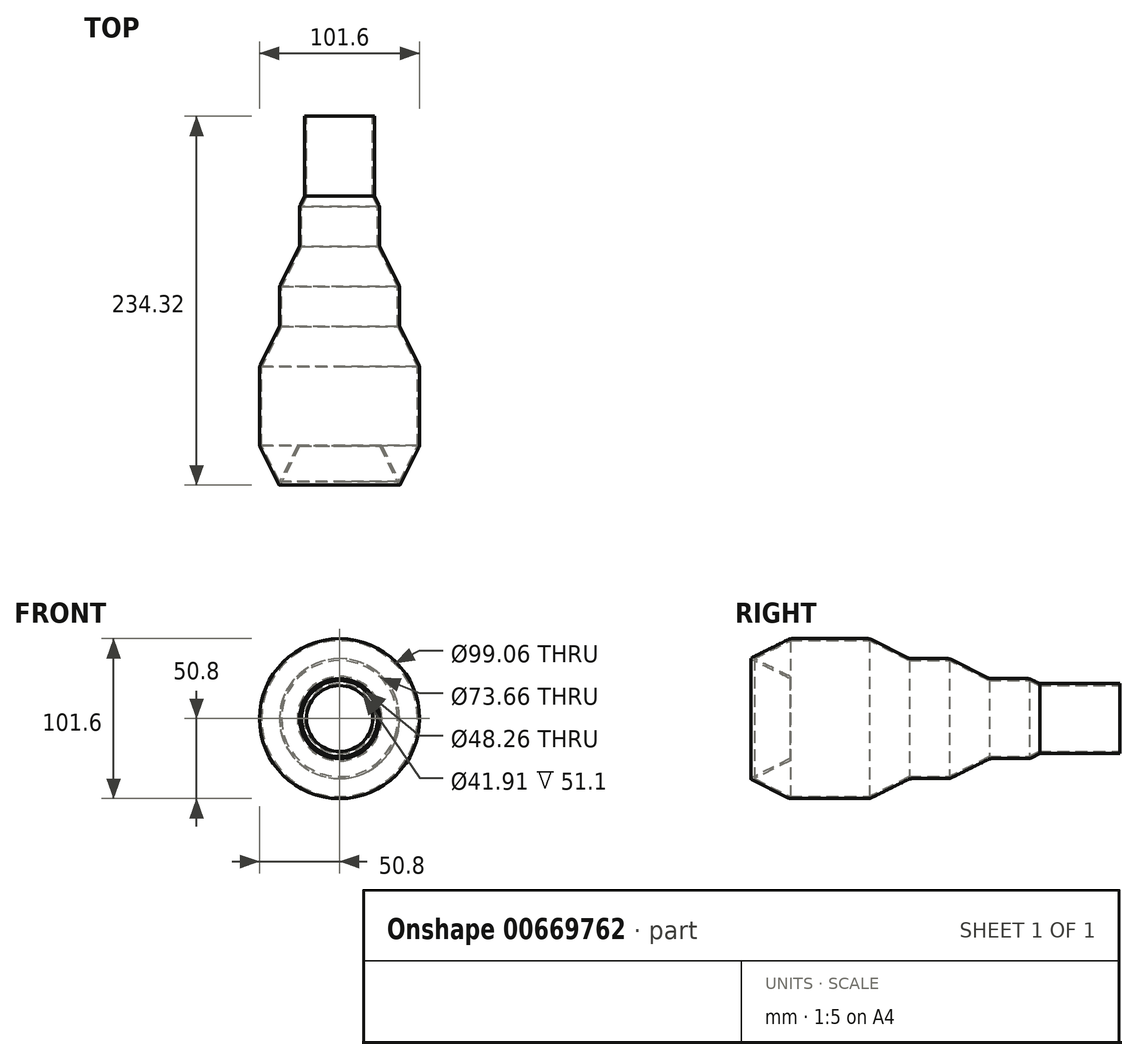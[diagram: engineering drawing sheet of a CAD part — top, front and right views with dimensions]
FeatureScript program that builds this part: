
annotation { "Feature Type Name" : "Feature", "Feature Type Description" : "" }
export const myFeature = defineFeature(function(context is Context, id is Id, definition is map)
    precondition{}
    {
        {
            var Q0;
            Q0=qCreatedBy(makeId("Right.planeOp"),FACE);
            var sketch = newSketch(context, id + "F0", { "sketchPlane" : qUnion([Q0])});
            skLineSegment(sketch, "E0", {"start": v(-199.49, 0) * mm, "end": v(219.8, 0) * mm, "construction": true});
            skLineSegment(sketch, "E1", {"start": v(-135.4, 50.8) * mm, "end": v(-84.6, 50.8) * mm});
            skLineSegment(sketch, "E2", {"start": v(-84.6, 50.8) * mm, "end": v(-59.2, 38.1) * mm});
            skLineSegment(sketch, "E3", {"start": v(-59.2, 38.1) * mm, "end": v(-33.8, 38.1) * mm});
            skLineSegment(sketch, "E4", {"start": v(-33.8, 38.1) * mm, "end": v(-8.4, 25.4) * mm});
            skLineSegment(sketch, "E5", {"start": v(-8.4, 25.4) * mm, "end": v(17, 25.4) * mm});
            skLineSegment(sketch, "E6", {"start": v(17, 25.4) * mm, "end": v(23.35, 22.23) * mm});
            skLineSegment(sketch, "E7", {"start": v(23.35, 22.23) * mm, "end": v(74.15, 22.23) * mm});
            skLineSegment(sketch, "E8", {"start": v(-135.4, 50.8) * mm, "end": v(-160.8, 38.1) * mm});
            skLineSegment(sketch, "E9", {"start": v(-160.8, 38.1) * mm, "end": v(-135.4, 25.4) * mm});
            skLineSegment(sketch, "E10", {"start": v(-84.6, 50.8) * mm, "end": v(-84.6, 0) * mm, "construction": true});
            skLineSegment(sketch, "E11", {"start": v(-59.2, 38.1) * mm, "end": v(-59.2, 0) * mm, "construction": true});
            skLineSegment(sketch, "E12", {"start": v(-33.8, 38.1) * mm, "end": v(-33.8, 0) * mm, "construction": true});
            skLineSegment(sketch, "E13", {"start": v(-8.4, 25.4) * mm, "end": v(-8.4, 0) * mm, "construction": true});
            skLineSegment(sketch, "E14", {"start": v(17, 25.4) * mm, "end": v(17, 0) * mm, "construction": true});
            skLineSegment(sketch, "E15", {"start": v(23.35, 22.23) * mm, "end": v(23.35, 0) * mm, "construction": true});
            skLineSegment(sketch, "E16", {"start": v(-135.4, 50.8) * mm, "end": v(-135.4, 0) * mm, "construction": true});
            skLineSegment(sketch, "E17", {"start": v(-160.8, 38.1) * mm, "end": v(-160.8, 0) * mm, "construction": true});
            skLineSegment(sketch, "E18", {"start": v(74.15, 22.23) * mm, "end": v(74.15, 0) * mm});
            skLineSegment(sketch, "E19.0", {"start": v(-157.96, 38.1) * mm, "end": v(-135.4, 26.82) * mm});
            skLineSegment(sketch, "E19.1", {"start": v(-135.1, 49.53) * mm, "end": v(-157.96, 38.1) * mm});
            skLineSegment(sketch, "E19.2", {"start": v(-135.1, 49.53) * mm, "end": v(-84.9, 49.53) * mm});
            skLineSegment(sketch, "E19.3", {"start": v(-84.9, 49.53) * mm, "end": v(-59.5, 36.83) * mm});
            skLineSegment(sketch, "E19.4", {"start": v(-59.5, 36.83) * mm, "end": v(-34.1, 36.83) * mm});
            skLineSegment(sketch, "E19.5", {"start": v(23.05, 20.95) * mm, "end": v(74.15, 20.95) * mm});
            skLineSegment(sketch, "E19.6", {"start": v(16.7, 24.13) * mm, "end": v(23.05, 20.95) * mm});
            skLineSegment(sketch, "E19.7", {"start": v(-8.7, 24.13) * mm, "end": v(16.7, 24.13) * mm});
            skLineSegment(sketch, "E19.8", {"start": v(-34.1, 36.83) * mm, "end": v(-8.7, 24.13) * mm});
            skLineSegment(sketch, "E20", {"start": v(-135.4, 26.82) * mm, "end": v(-135.4, 25.4) * mm});
            skLineSegment(sketch, "E21.MirrorCS", {"start": v(16.7, -24.13) * mm, "end": v(23.05, -20.95) * mm});
            skLineSegment(sketch, "E22.MirrorCS", {"start": v(17, -25.4) * mm, "end": v(23.35, -22.22) * mm});
            skLineSegment(sketch, "E23.MirrorCS", {"start": v(-135.4, -26.82) * mm, "end": v(-135.4, -25.4) * mm});
            skLineSegment(sketch, "E24.MirrorCS", {"start": v(-135.1, -49.53) * mm, "end": v(-157.96, -38.1) * mm});
            skLineSegment(sketch, "E25.MirrorCS", {"start": v(-84.9, -49.53) * mm, "end": v(-59.5, -36.83) * mm});
            skLineSegment(sketch, "E26.MirrorCS", {"start": v(-59.5, -36.83) * mm, "end": v(-34.1, -36.83) * mm});
            skLineSegment(sketch, "E27.MirrorCS", {"start": v(-34.1, -36.83) * mm, "end": v(-8.7, -24.13) * mm});
            skLineSegment(sketch, "E28.MirrorCS", {"start": v(-135.4, -50.8) * mm, "end": v(-160.8, -38.1) * mm});
            skLineSegment(sketch, "E29.MirrorCS", {"start": v(-160.8, -38.1) * mm, "end": v(-135.4, -25.4) * mm});
            skLineSegment(sketch, "E30.MirrorCS", {"start": v(23.35, -22.23) * mm, "end": v(74.15, -22.23) * mm});
            skLineSegment(sketch, "E31.MirrorCS", {"start": v(-59.2, -38.1) * mm, "end": v(-33.8, -38.1) * mm});
            skLineSegment(sketch, "E32.MirrorCS", {"start": v(-33.8, -38.1) * mm, "end": v(-8.4, -25.4) * mm});
            skLineSegment(sketch, "E33.MirrorCS", {"start": v(-8.4, -25.4) * mm, "end": v(17, -25.4) * mm});
            skLineSegment(sketch, "E34.MirrorCS", {"start": v(-135.4, -50.8) * mm, "end": v(-84.6, -50.8) * mm});
            skLineSegment(sketch, "E35.MirrorCS", {"start": v(-84.6, -50.8) * mm, "end": v(-59.2, -38.1) * mm});
            skLineSegment(sketch, "E36.MirrorCS", {"start": v(-8.7, -24.13) * mm, "end": v(16.7, -24.13) * mm});
            skLineSegment(sketch, "E37.MirrorCS", {"start": v(-157.96, -38.1) * mm, "end": v(-135.4, -26.82) * mm});
            skLineSegment(sketch, "E38.MirrorCS", {"start": v(23.05, -20.95) * mm, "end": v(74.15, -20.95) * mm});
            skLineSegment(sketch, "E39.MirrorCS", {"start": v(-135.1, -49.53) * mm, "end": v(-84.9, -49.53) * mm});
            skLineSegment(sketch, "E40.MirrorCS", {"start": v(74.15, -22.23) * mm, "end": v(74.15, 0) * mm});
            skLineSegment(sketch, "E41", {"start": v(74.15, 20.95) * mm, "end": v(74.15, 20.95) * mm});
            skSolve(sketch);
        }
        {
            var Q0;
            Q0=qCreatedBy(makeId("Front.planeOp"),FACE);
            var sketch = newSketch(context, id + "F1", { "sketchPlane" : qUnion([Q0])});
            skCircle(sketch, "E42", {"center": v(0, 0) * mm, "radius": 50.8 * mm});
            skCircle(sketch, "E43.0", {"center": v(0, 0) * mm, "radius": 50.04 * mm});
            skSolve(sketch);
        }
        {
            var Q0;
            Q0 = qSketchRegion(id + "F0", true);
            var Q1;
            Q1=sQuery(id+"F1.wireOp",EDGE,"E43.0");
            revolve(context, id + "F2", {"entities" : qUnion([Q0]), "axis" : qUnion([Q1]), "revolveType" : RevolveType.FULL});
        }
        {
            var Q0;
            Q0=makeQuery(id+"F2.opRevolve","SWEPT_BODY",BODY,{"disambiguationData":[OSD([sQuery(id+"F0.wireOp",EDGE,"E21.MirrorCS"),sQuery(id+"F0.wireOp",EDGE,"E22.MirrorCS"),sQuery(id+"F0.wireOp",EDGE,"E23.MirrorCS"),sQuery(id+"F0.wireOp",EDGE,"E24.MirrorCS"),sQuery(id+"F0.wireOp",EDGE,"E25.MirrorCS"),sQuery(id+"F0.wireOp",EDGE,"E26.MirrorCS"),sQuery(id+"F0.wireOp",EDGE,"E27.MirrorCS"),sQuery(id+"F0.wireOp",EDGE,"E28.MirrorCS"),sQuery(id+"F0.wireOp",EDGE,"E29.MirrorCS"),sQuery(id+"F0.wireOp",EDGE,"E30.MirrorCS"),sQuery(id+"F0.wireOp",EDGE,"E31.MirrorCS"),sQuery(id+"F0.wireOp",EDGE,"E32.MirrorCS"),sQuery(id+"F0.wireOp",EDGE,"E33.MirrorCS"),sQuery(id+"F0.wireOp",EDGE,"E34.MirrorCS"),sQuery(id+"F0.wireOp",EDGE,"E35.MirrorCS"),sQuery(id+"F0.wireOp",EDGE,"E36.MirrorCS"),sQuery(id+"F0.wireOp",EDGE,"E37.MirrorCS"),sQuery(id+"F0.wireOp",EDGE,"E38.MirrorCS"),sQuery(id+"F0.wireOp",EDGE,"E39.MirrorCS"),sQuery(id+"F0.wireOp",EDGE,"E40.MirrorCS")])]});
            deleteBodies(context, id + "F3", {"entities" : qUnion([Q0])});
        }
        {
            var Q0;
            Q0=makeQuery(id+"F2.opRevolve","SWEPT_EDGE",EDGE,{"disambiguationData":[OSD([sQuery(id+"F0.wireOp",EDGE,"E1"),sQuery(id+"F0.wireOp",EDGE,"E8")])]});
            var Q1;
            Q1=makeQuery(id+"F2.opRevolve","SWEPT_EDGE",EDGE,{"disambiguationData":[OSD([sQuery(id+"F0.wireOp",EDGE,"E1"),sQuery(id+"F0.wireOp",EDGE,"E2")])]});
            var Q2;
            Q2=makeQuery(id+"F2.opRevolve","SWEPT_EDGE",EDGE,{"disambiguationData":[OSD([sQuery(id+"F0.wireOp",EDGE,"E3"),sQuery(id+"F0.wireOp",EDGE,"E4")])]});
            var Q3;
            Q3=makeQuery(id+"F2.opRevolve","SWEPT_EDGE",EDGE,{"disambiguationData":[OSD([sQuery(id+"F0.wireOp",EDGE,"E5"),sQuery(id+"F0.wireOp",EDGE,"E6")])]});
            fillet(context, id + "F4", {"entities" : qUnion([Q0, Q1, Q2, Q3]), "radius" : 5.08 * mm, "tangentPropagation" : true, "allowEdgeOverflow" : false});
        }
        {
            var Q0;
            Q0=makeQuery(id+"F2.opRevolve","SWEPT_EDGE",EDGE,{"disambiguationData":[OSD([sQuery(id+"F0.wireOp",EDGE,"E4"),sQuery(id+"F0.wireOp",EDGE,"E5")])]});
            var Q1;
            Q1=makeQuery(id+"F2.opRevolve","SWEPT_EDGE",EDGE,{"disambiguationData":[OSD([sQuery(id+"F0.wireOp",EDGE,"E2"),sQuery(id+"F0.wireOp",EDGE,"E3")])]});
            fillet(context, id + "F5", {"entities" : qUnion([Q0, Q1]), "radius" : 5.08 * mm, "tangentPropagation" : true, "allowEdgeOverflow" : false});
        }
        {
            var Q0;
            Q0=makeQuery(id+"F2.opRevolve","SWEPT_EDGE",EDGE,{"disambiguationData":[OSD([sQuery(id+"F0.wireOp",EDGE,"E8"),sQuery(id+"F0.wireOp",EDGE,"E9")])]});
            fillet(context, id + "F6", {"entities" : qUnion([Q0]), "radius" : 0.5 * mm, "tangentPropagation" : true, "allowEdgeOverflow" : false});
        }
    });
